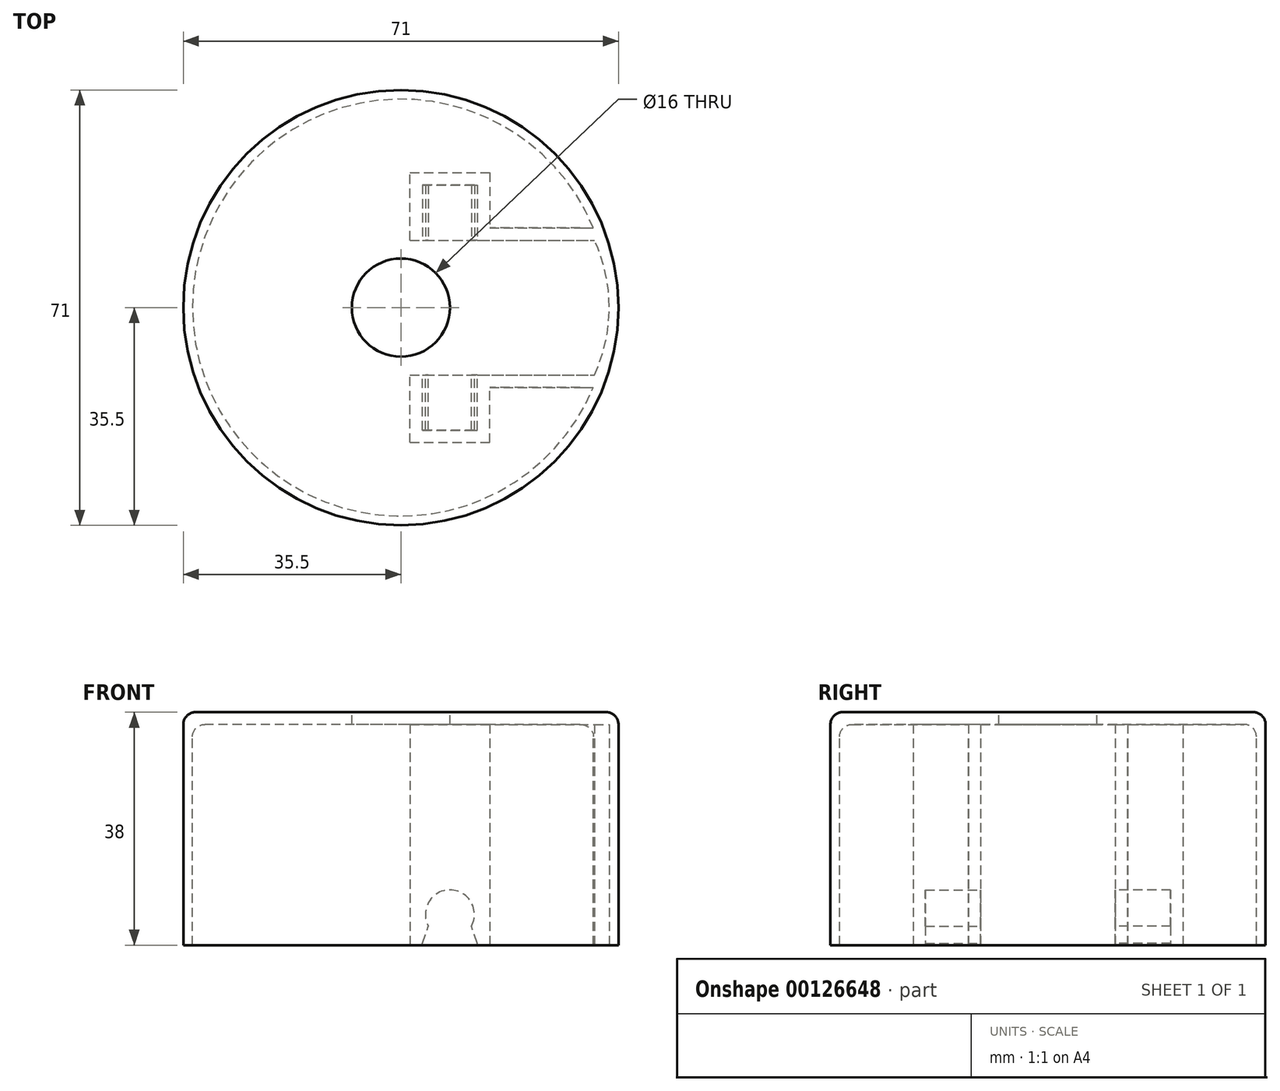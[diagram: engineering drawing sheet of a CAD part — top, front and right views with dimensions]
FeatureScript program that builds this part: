
annotation { "Feature Type Name" : "Feature", "Feature Type Description" : "" }
export const myFeature = defineFeature(function(context is Context, id is Id, definition is map)
    precondition{}
    {
        {
            var Q0;
            Q0=qCreatedBy(makeId("Front.planeOp"),FACE);
            var sketch = newSketch(context, id + "F0", { "sketchPlane" : qUnion([Q0])});
            skLineSegment(sketch, "E0", {"start": v(27.5, -5) * mm, "end": v(27.5, 31) * mm});
            skLineSegment(sketch, "E1", {"start": v(27.5, 31) * mm, "end": v(0, 31) * mm});
            skLineSegment(sketch, "E2", {"start": v(0, 26) * mm, "end": v(0, 31) * mm});
            skLineSegment(sketch, "E3", {"start": v(26, 0) * mm, "end": v(26, -5) * mm});
            skLineSegment(sketch, "E4", {"start": v(26, -5) * mm, "end": v(27.5, -5) * mm});
            skLineSegment(sketch, "E5", {"start": v(0, 26) * mm, "end": v(26, 26) * mm});
            skLineSegment(sketch, "E6", {"start": v(26, 26) * mm, "end": v(26, 0) * mm});
            skSolve(sketch);
        }
        {
            var Q0;
            Q0 = qSketchRegion(id + "F0", true);
            var Q1;
            Q1=sQuery(id+"F0.wireOp",EDGE,"E2");
            revolve(context, id + "F1", {"entities" : qUnion([Q0]), "axis" : qUnion([Q1]), "revolveType" : RevolveType.FULL});
        }
        {
            var Q0;
            Q0=makeQuery(id+"F1.opRevolve","SWEPT_FACE",FACE,{"disambiguationData":[OSD([sQuery(id+"F0.wireOp",EDGE,"E4")])]});
            var sketch = newSketch(context, id + "F2", { "sketchPlane" : qUnion([Q0])});
            skArc(sketch, "E7.0", {"start": v(23.56, 11) * mm, "mid": v(0, 26) * mm, "end": v(-23.56, 11) * mm});
            skLineSegment(sketch, "E8", {"start": v(-23.56, 11) * mm, "end": v(23.56, 11) * mm});
            skLineSegment(sketch, "E9", {"start": v(0, 0) * mm, "end": v(20.46, 0) * mm, "construction": true});
            skLineSegment(sketch, "E10.MirrorCS", {"start": v(-23.56, -11) * mm, "end": v(23.56, -11) * mm});
            skArc(sketch, "E11.MirrorCS", {"start": v(23.56, -11) * mm, "mid": v(0, -26) * mm, "end": v(-23.56, -11) * mm});
            skSolve(sketch);
        }
        {
            var Q0;
            Q0 = qSketchRegion(id + "F2", true);
            var Q1;
            Q1=makeQuery(id+"F1.opRevolve","SWEPT_FACE",FACE,{"disambiguationData":[OSD([sQuery(id+"F0.wireOp",EDGE,"E1")])]});
            extrude(context, id + "F3", {"entities" : qUnion([Q0]), "operationType" : NewBodyOperationType.ADD, "endBound" : BoundingType.UP_TO_SURFACE, "oppositeDirection" : true, "endBoundEntityFace" : qUnion([Q1]), "depth" : 25 * mm});
        }
        {
            var Q0;
            Q0=qCreatedBy(makeId("Front.planeOp"),FACE);
            var sketch = newSketch(context, id + "F4", { "sketchPlane" : qUnion([Q0])});
            skArc(sketch, "E12", {"start": v(3.5, -1.94) * mm, "mid": v(3.45, 2.03) * mm, "end": v(0, 4) * mm});
            skLineSegment(sketch, "E13", {"start": v(3.5, -1.94) * mm, "end": v(4.5, -4.68) * mm});
            skLineSegment(sketch, "E14", {"start": v(4.5, -4.68) * mm, "end": v(4.5, -5) * mm});
            skLineSegment(sketch, "E15", {"start": v(0, -5) * mm, "end": v(0, 4) * mm, "construction": true});
            skLineSegment(sketch, "E16", {"start": v(4, -11.62) * mm, "end": v(4, 7.64) * mm, "construction": true});
            skLineSegment(sketch, "E17", {"start": v(4.5, -5) * mm, "end": v(0, -5) * mm});
            skArc(sketch, "E18.MirrorCS", {"start": v(-3.5, -1.94) * mm, "mid": v(-3.45, 2.03) * mm, "end": v(0, 4) * mm});
            skLineSegment(sketch, "E19.MirrorCS", {"start": v(-3.5, -1.94) * mm, "end": v(-4.5, -4.68) * mm});
            skLineSegment(sketch, "E20.MirrorCS", {"start": v(-4.5, -4.68) * mm, "end": v(-4.5, -5) * mm});
            skLineSegment(sketch, "E21.MirrorCS", {"start": v(-4.5, -5) * mm, "end": v(0, -5) * mm});
            skSolve(sketch);
        }
        {
            var Q0;
            Q0 = qSketchRegion(id + "F4", true);
            extrude(context, id + "F5", {"entities" : qUnion([Q0]), "operationType" : NewBodyOperationType.REMOVE, "endBound" : BoundingType.SYMMETRIC, "oppositeDirection" : true, "depth" : 40 * mm});
        }
        {
            var Q0;
            Q0=makeQuery(id+"F3.boolean.opBoolean","MERGE",FACE,{"derivedFrom":[makeQuery(id+"F1.opRevolve","SWEPT_FACE",FACE,{"disambiguationData":[OSD([sQuery(id+"F0.wireOp",EDGE,"E4")])]}),makeQuery(id+"F3.opExtrude","CAP_FACE",FACE,{"disambiguationData":[OSD([sQuery(id+"F2.wireOp",EDGE,"E7.0"),sQuery(id+"F2.wireOp",EDGE,"E8")])],"isStart":true}),makeQuery(id+"F3.opExtrude","CAP_FACE",FACE,{"disambiguationData":[OSD([sQuery(id+"F2.wireOp",EDGE,"E10.MirrorCS"),sQuery(id+"F2.wireOp",EDGE,"E11.MirrorCS")])],"isStart":true})]});
            var sketch = newSketch(context, id + "F6", { "sketchPlane" : qUnion([Q0])});
            skLineSegment(sketch, "E22.0", {"start": v(6.5, -13) * mm, "end": v(24.23, -13) * mm});
            skLineSegment(sketch, "E22.1", {"start": v(-24.23, -13) * mm, "end": v(-6.5, -13) * mm});
            skLineSegment(sketch, "E22.2", {"start": v(-6.5, -22) * mm, "end": v(-6.5, -13) * mm});
            skLineSegment(sketch, "E22.3", {"start": v(-6.5, -22) * mm, "end": v(6.5, -22) * mm});
            skLineSegment(sketch, "E22.4", {"start": v(6.5, -22) * mm, "end": v(6.5, -13) * mm});
            skArc(sketch, "E23.0", {"start": v(-24.23, -13) * mm, "mid": v(0, -27.5) * mm, "end": v(24.23, -13) * mm});
            skLineSegment(sketch, "E24", {"start": v(0, 0) * mm, "end": v(-27.5, 0) * mm, "construction": true});
            skPoint(sketch, "E24.endSnap0", {"position": v(-26, 0) * mm});
            skLineSegment(sketch, "E25.MirrorCS", {"start": v(6.5, 13) * mm, "end": v(24.23, 13) * mm});
            skArc(sketch, "E26.MirrorCS", {"start": v(-24.23, 13) * mm, "mid": v(0, 27.5) * mm, "end": v(24.23, 13) * mm});
            skLineSegment(sketch, "E27.MirrorCS", {"start": v(-24.23, 13) * mm, "end": v(-6.5, 13) * mm});
            skLineSegment(sketch, "E28.MirrorCS", {"start": v(-6.5, 22) * mm, "end": v(-6.5, 13) * mm});
            skLineSegment(sketch, "E29.MirrorCS", {"start": v(-6.5, 22) * mm, "end": v(6.5, 22) * mm});
            skLineSegment(sketch, "E30.MirrorCS", {"start": v(6.5, 22) * mm, "end": v(6.5, 13) * mm});
            skSolve(sketch);
        }
        {
            var Q0;
            Q0 = qSketchRegion(id + "F6", true);
            extrude(context, id + "F7", {"entities" : qUnion([Q0]), "operationType" : NewBodyOperationType.REMOVE, "endBound" : BoundingType.THROUGH_ALL, "oppositeDirection" : true, "depth" : 25 * mm});
        }
        {
            var Q0;
            Q0=qCreatedBy(makeId("Front.planeOp"),FACE);
            var sketch = newSketch(context, id + "F8", { "sketchPlane" : qUnion([Q0])});
            skLineSegment(sketch, "E31", {"start": v(27.5, -5) * mm, "end": v(27.5, 33) * mm});
            skLineSegment(sketch, "E32", {"start": v(27.5, 33) * mm, "end": v(-8, 33) * mm});
            skLineSegment(sketch, "E33", {"start": v(-8, 33) * mm, "end": v(-8, 31) * mm});
            skLineSegment(sketch, "E34", {"start": v(-8, 31) * mm, "end": v(26, 31) * mm});
            skLineSegment(sketch, "E35", {"start": v(26, 31) * mm, "end": v(26, -5) * mm});
            skLineSegment(sketch, "E36", {"start": v(23.56, -5) * mm, "end": v(26, -5) * mm});
            skLineSegment(sketch, "E37.0", {"start": v(26, -5) * mm, "end": v(27.5, -5) * mm});
            skPoint(sketch, "E38.orphan", {"position": v(26, -5) * mm});
            skSolve(sketch);
        }
        {
            var Q0;
            Q0 = qSketchRegion(id + "F8", true);
            var Q1;
            Q1=sQuery(id+"F8.wireOp",EDGE,"E33");
            revolve(context, id + "F9", {"operationType" : NewBodyOperationType.ADD, "entities" : qUnion([Q0]), "axis" : qUnion([Q1]), "revolveType" : RevolveType.FULL});
        }
        {
            var Q0;
            Q0=makeQuery(id+"F9.opRevolve","SWEPT_FACE",FACE,{"disambiguationData":[OSD([sQuery(id+"F8.wireOp",EDGE,"E32")])]});
            var sketch = newSketch(context, id + "F10", { "sketchPlane" : qUnion([Q0])});
            skCircle(sketch, "E39", {"center": v(-8, 0) * mm, "radius": 10 * mm});
            skSolve(sketch);
        }
        {
            var Q0;
            Q0 = qSketchRegion(id + "F10", true);
            var Q1;
            Q1=makeQuery(id+"F1.opRevolve","SWEPT_FACE",FACE,{"disambiguationData":[OSD([sQuery(id+"F0.wireOp",EDGE,"E5")])]});
            extrude(context, id + "F11", {"entities" : qUnion([Q0]), "operationType" : NewBodyOperationType.REMOVE, "endBound" : BoundingType.UP_TO_SURFACE, "oppositeDirection" : true, "endBoundEntityFace" : qUnion([Q1]), "depth" : 5 * mm});
        }
        {
            var Q0;
            Q0=makeQuery(id+"F9.opRevolve","SWEPT_FACE",FACE,{"disambiguationData":[OSD([sQuery(id+"F8.wireOp",EDGE,"E32")])]});
            var sketch = newSketch(context, id + "F12", { "sketchPlane" : qUnion([Q0])});
            skCircle(sketch, "E40", {"center": v(-8, 0) * mm, "radius": 8 * mm});
            skCircle(sketch, "E41.0", {"center": v(-8, 0) * mm, "radius": 10 * mm});
            skSolve(sketch);
        }
        {
            var Q0;
            Q0 = qSketchRegion(id + "F12", true);
            extrude(context, id + "F13", {"entities" : qUnion([Q0]), "operationType" : NewBodyOperationType.ADD, "oppositeDirection" : true, "depth" : 2 * mm});
        }
        {
            var Q0;
            Q0=makeQuery(id+"F9.opRevolve","SWEPT_FACE",FACE,{"disambiguationData":[OSD([sQuery(id+"F8.wireOp",EDGE,"E32")])]});
            var sketch = newSketch(context, id + "F14", { "sketchPlane" : qUnion([Q0])});
            skLineSegment(sketch, "E42.bottom", {"start": v(-56.72, 0) * mm, "end": v(56.8, 0) * mm});
            skLineSegment(sketch, "E42.top", {"start": v(-56.72, -51.09) * mm, "end": v(56.8, -51.09) * mm});
            skLineSegment(sketch, "E42.left", {"start": v(-56.72, 0) * mm, "end": v(-56.72, -51.09) * mm});
            skLineSegment(sketch, "E42.right", {"start": v(56.8, 0) * mm, "end": v(56.8, -51.09) * mm});
            skSolve(sketch);
        }
        {
            var Q0;
            Q0 = qSketchRegion(id + "F14", true);
            extrude(context, id + "F15", {"entities" : qUnion([Q0]), "operationType" : NewBodyOperationType.REMOVE, "endBound" : BoundingType.THROUGH_ALL, "oppositeDirection" : true, "depth" : 25 * mm});
        }
        {
            var Q0;
            Q0=makeQuery(id+"F9.boolean.opBoolean","MERGE",FACE,{"derivedFrom":[makeQuery(id+"F3.boolean.opBoolean","MERGE",FACE,{"derivedFrom":[makeQuery(id+"F1.opRevolve","SWEPT_FACE",FACE,{"disambiguationData":[OSD([sQuery(id+"F0.wireOp",EDGE,"E4")])]}),makeQuery(id+"F3.opExtrude","CAP_FACE",FACE,{"disambiguationData":[OSD([sQuery(id+"F2.wireOp",EDGE,"E7.0"),sQuery(id+"F2.wireOp",EDGE,"E8")])],"isStart":true}),makeQuery(id+"F3.opExtrude","CAP_FACE",FACE,{"disambiguationData":[OSD([sQuery(id+"F2.wireOp",EDGE,"E10.MirrorCS"),sQuery(id+"F2.wireOp",EDGE,"E11.MirrorCS")])],"isStart":true})]}),makeQuery(id+"F9.opRevolve","SWEPT_FACE",FACE,{"disambiguationData":[OSD([sQuery(id+"F8.wireOp",EDGE,"E37.0")])]})]});
            var sketch = newSketch(context, id + "F16", { "sketchPlane" : qUnion([Q0])});
            skLineSegment(sketch, "E43.bottom", {"start": v(-6.5, -13) * mm, "end": v(-33.24, -13) * mm});
            skLineSegment(sketch, "E43.top", {"start": v(-6.5, 11.31) * mm, "end": v(-33.24, 11.31) * mm});
            skLineSegment(sketch, "E43.left", {"start": v(-6.5, -13) * mm, "end": v(-6.5, 11.31) * mm});
            skLineSegment(sketch, "E43.right", {"start": v(-33.24, -13) * mm, "end": v(-33.24, 11.31) * mm});
            skSolve(sketch);
        }
        {
            var Q0;
            Q0 = qSketchRegion(id + "F16", true);
            var Q1;
            Q1=makeQuery(id+"F9.opRevolve","SWEPT_FACE",FACE,{"disambiguationData":[OSD([sQuery(id+"F8.wireOp",EDGE,"E34")])]});
            extrude(context, id + "F17", {"entities" : qUnion([Q0]), "operationType" : NewBodyOperationType.REMOVE, "endBound" : BoundingType.UP_TO_SURFACE, "oppositeDirection" : true, "endBoundEntityFace" : qUnion([Q1]), "depth" : 25 * mm});
        }
        {
            var Q0;
            Q0=makeQuery(id+"F9.opRevolve","SWEPT_EDGE",EDGE,{"disambiguationData":[OSD([sQuery(id+"F8.wireOp",EDGE,"E34"),sQuery(id+"F8.wireOp",EDGE,"E35")])]});
            var Q1;
            {var subQ0=sQuery(id+"F0.wireOp",EDGE,"E0");var subQ1=sQuery(id+"F0.wireOp",EDGE,"E1");Q1=makeQuery(id+"F7.boolean.opBoolean","SPLIT",EDGE,{"disambiguationData":[TD([makeQuery(id+"F7.opExtrude","SWEPT_FACE",FACE,{"disambiguationData":[OSD([sQuery(id+"F6.wireOp",EDGE,"E22.1")])]})])],"derivedFrom":makeQuery(id+"F1.opRevolve","SWEPT_EDGE",EDGE,{"disambiguationData":[OSD([subQ0,subQ1])]})});}
            var Q2;
            Q2=makeQuery(id+"F9.opRevolve","SWEPT_EDGE",EDGE,{"disambiguationData":[OSD([sQuery(id+"F8.wireOp",EDGE,"E31"),sQuery(id+"F8.wireOp",EDGE,"E32")])]});
            var Q3;
            Q3=makeQuery(id+"F7.boolean.opBoolean","INTERSECT",EDGE,{"derivedFrom":[makeQuery(id+"F1.opRevolve","SWEPT_FACE",FACE,{"disambiguationData":[OSD([sQuery(id+"F0.wireOp",EDGE,"E1")])]}),makeQuery(id+"F7.opExtrude","SWEPT_FACE",FACE,{"disambiguationData":[OSD([sQuery(id+"F6.wireOp",EDGE,"E22.1")])]})]});
            var Q4;
            Q4=makeQuery(id+"F7.boolean.opBoolean","INTERSECT",EDGE,{"derivedFrom":[makeQuery(id+"F1.opRevolve","SWEPT_FACE",FACE,{"disambiguationData":[OSD([sQuery(id+"F0.wireOp",EDGE,"E1")])]}),makeQuery(id+"F7.opExtrude","SWEPT_FACE",FACE,{"disambiguationData":[OSD([sQuery(id+"F6.wireOp",EDGE,"E22.2")])]})]});
            var Q5;
            Q5=makeQuery(id+"F7.boolean.opBoolean","INTERSECT",EDGE,{"derivedFrom":[makeQuery(id+"F1.opRevolve","SWEPT_FACE",FACE,{"disambiguationData":[OSD([sQuery(id+"F0.wireOp",EDGE,"E1")])]}),makeQuery(id+"F7.opExtrude","SWEPT_FACE",FACE,{"disambiguationData":[OSD([sQuery(id+"F6.wireOp",EDGE,"E22.3")])]})]});
            var Q6;
            Q6=makeQuery(id+"F7.boolean.opBoolean","INTERSECT",EDGE,{"derivedFrom":[makeQuery(id+"F1.opRevolve","SWEPT_FACE",FACE,{"disambiguationData":[OSD([sQuery(id+"F0.wireOp",EDGE,"E1")])]}),makeQuery(id+"F7.opExtrude","SWEPT_FACE",FACE,{"disambiguationData":[OSD([sQuery(id+"F6.wireOp",EDGE,"E22.4")])]})]});
            var Q7;
            Q7=makeQuery(id+"F7.boolean.opBoolean","INTERSECT",EDGE,{"derivedFrom":[makeQuery(id+"F1.opRevolve","SWEPT_FACE",FACE,{"disambiguationData":[OSD([sQuery(id+"F0.wireOp",EDGE,"E1")])]}),makeQuery(id+"F7.opExtrude","SWEPT_FACE",FACE,{"disambiguationData":[OSD([sQuery(id+"F6.wireOp",EDGE,"E22.0")])]})]});
            fillet(context, id + "F18", {"entities" : qUnion([Q0, Q1, Q2, Q3, Q4, Q5, Q6, Q7]), "radius" : 2 * mm, "tangentPropagation" : true, "allowEdgeOverflow" : false});
        }
        {
            var Q0;
            Q0=makeQuery(id+"F1.opRevolve","SWEPT_FACE",FACE,{"disambiguationData":[OSD([sQuery(id+"F0.wireOp",EDGE,"E5")])]});
            var sketch = newSketch(context, id + "F19", { "sketchPlane" : qUnion([Q0])});
            skLineSegment(sketch, "E44.0.0", {"start": v(-6.5, -9.89) * mm, "end": v(-6.5, -11) * mm});
            skLineSegment(sketch, "E44.0.1", {"start": v(-6.5, -11) * mm, "end": v(23.56, -11) * mm});
            skArc(sketch, "E44.0.2", {"start": v(23.56, -11) * mm, "mid": v(25.38, -5.63) * mm, "end": v(26, 0) * mm});
            skLineSegment(sketch, "E44.0.3", {"start": v(26, 0) * mm, "end": v(2, 0) * mm});
            skArc(sketch, "E44.0.4", {"start": v(2, 0) * mm, "mid": v(-0.42, -6.52) * mm, "end": v(-6.5, -9.89) * mm});
            skSolve(sketch);
        }
        {
            var Q0;
            Q0 = qSketchRegion(id + "F19", true);
            var Q1;
            {var subQ0=sQuery(id+"F8.wireOp",EDGE,"E34");Q1=makeQuery(id+"F17.boolean.opBoolean","MERGE",FACE,{"derivedFrom":[makeQuery(id+"F9.opRevolve","SWEPT_FACE",FACE,{"disambiguationData":[OSD([subQ0])]}),makeQuery(id+"F13.opExtrude","CAP_FACE",FACE,{"disambiguationData":[OSD([sQuery(id+"F12.wireOp",EDGE,"E40"),sQuery(id+"F12.wireOp",EDGE,"E41.0")])],"isStart":false}),makeQuery(id+"F17.opExtrude","CAP_FACE",FACE,{"disambiguationData":[OSD([subQ0])],"isStart":false})]});}
            extrude(context, id + "F20", {"entities" : qUnion([Q0]), "operationType" : NewBodyOperationType.REMOVE, "endBound" : BoundingType.UP_TO_SURFACE, "oppositeDirection" : true, "endBoundEntityFace" : qUnion([Q1]), "depth" : 25 * mm});
        }
        {
            var Q0;
            Q0=makeQuery(id+"F1.opRevolve","SWEPT_BODY",BODY,{"disambiguationData":[OSD([sQuery(id+"F0.wireOp",EDGE,"vsk5nwtv-qj0M-SwkP-SLCN-qHQLpZN8fkFC"),sQuery(id+"F0.wireOp",EDGE,"E0"),sQuery(id+"F0.wireOp",EDGE,"E1"),sQuery(id+"F0.wireOp",EDGE,"E2"),sQuery(id+"F0.wireOp",EDGE,"E3"),sQuery(id+"F0.wireOp",EDGE,"E4")])]});
            var Q1;
            Q1=makeQuery(id+"F15.boolean.opBoolean","COPY",FACE,{"derivedFrom":makeQuery(id+"F15.opExtrude","SWEPT_FACE",FACE,{"disambiguationData":[OSD([sQuery(id+"F14.wireOp",EDGE,"E42.bottom")])]})});
            mirror(context, id + "F21", {"operationType" : NewBodyOperationType.ADD, "entities" : qUnion([Q0]), "mirrorPlane" : qUnion([Q1])});
        }
    });
